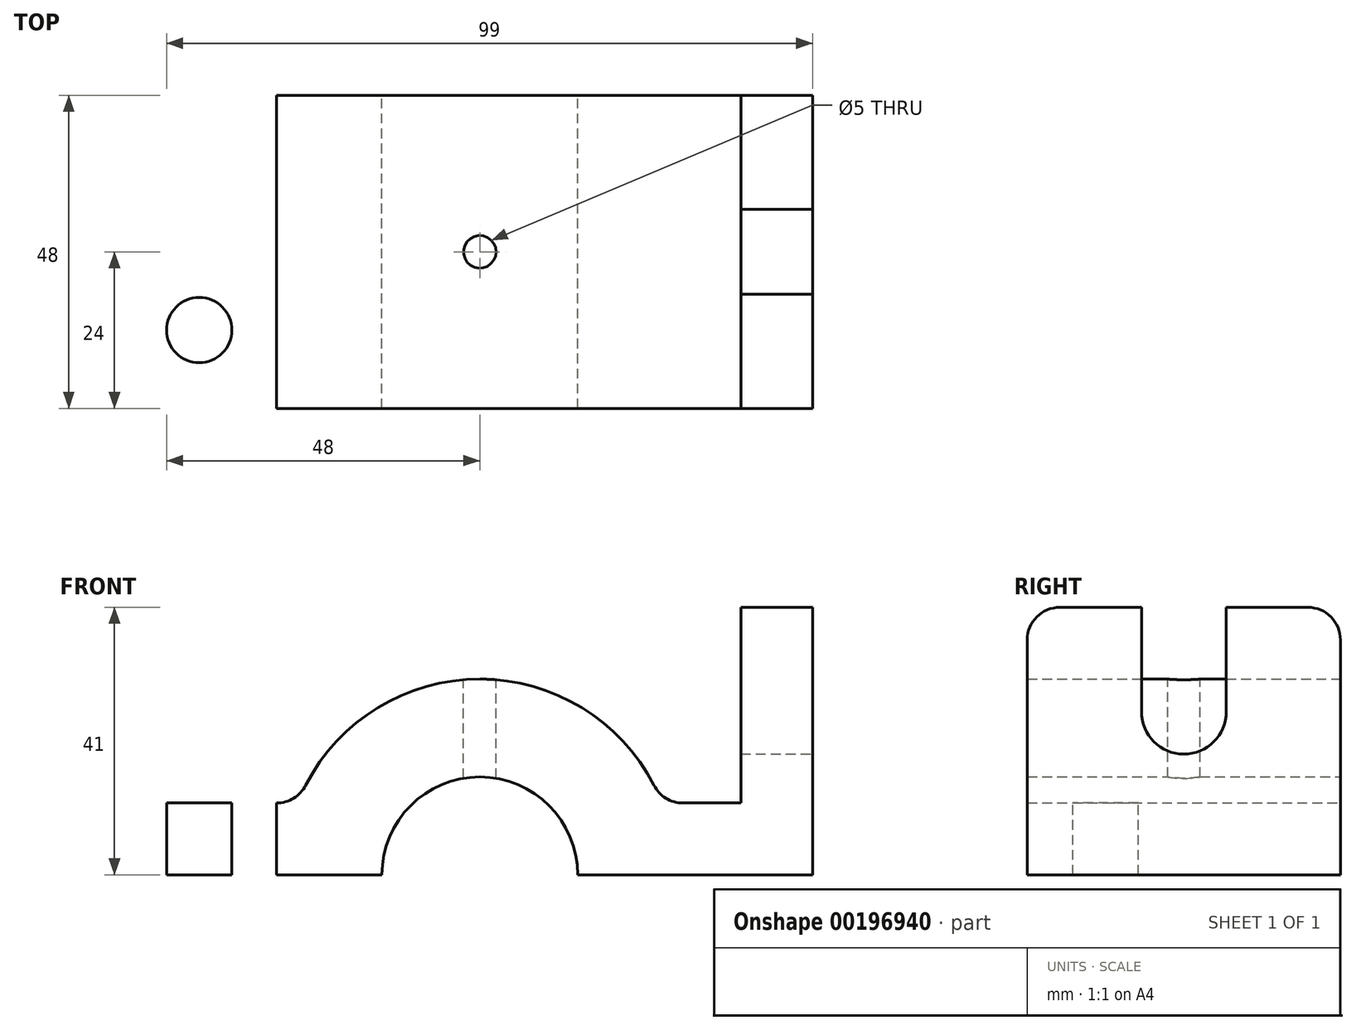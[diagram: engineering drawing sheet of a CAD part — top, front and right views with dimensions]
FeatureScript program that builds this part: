
annotation { "Feature Type Name" : "Feature", "Feature Type Description" : "" }
export const myFeature = defineFeature(function(context is Context, id is Id, definition is map)
    precondition{}
    {
        {
            var Q0;
            Q0=qCreatedBy(makeId("Front.planeOp"),FACE);
            var sketch = newSketch(context, id + "F0", { "sketchPlane" : qUnion([Q0])});
            skArc(sketch, "E0", {"start": v(15, 0) * mm, "mid": v(0, 15) * mm, "end": v(-15, 0) * mm});
            skArc(sketch, "E1", {"start": v(27.91, 11) * mm, "mid": v(0, 30) * mm, "end": v(-27.91, 11) * mm});
            skLineSegment(sketch, "E2", {"start": v(-15, 0) * mm, "end": v(-56, 0) * mm});
            skLineSegment(sketch, "E3", {"start": v(-56, 0) * mm, "end": v(-56, 11) * mm});
            skLineSegment(sketch, "E4", {"start": v(15, 0) * mm, "end": v(51, 0) * mm});
            skLineSegment(sketch, "E5", {"start": v(51, 0) * mm, "end": v(51, 41) * mm});
            skLineSegment(sketch, "E6", {"start": v(51, 41) * mm, "end": v(40, 41) * mm});
            skLineSegment(sketch, "E7", {"start": v(40, 41) * mm, "end": v(40, 11) * mm});
            skLineSegment(sketch, "E8", {"start": v(-56, 11) * mm, "end": v(-27.91, 11) * mm});
            skLineSegment(sketch, "E9.trimOffspring", {"start": v(27.91, 11) * mm, "end": v(40, 11) * mm});
            skSolve(sketch);
        }
        {
            var Q0;
            Q0=makeQuery(id+"F0.imprint","IMPRINT",FACE,{"disambiguationData":[TD([[makeQuery(id+"F0.imprint","IMPRINT",EDGE,{"derivedFrom":sQuery(id+"F0.wireOp",EDGE,"E0")}),-1.0]])]});
            extrude(context, id + "F1", {"entities" : qUnion([Q0]), "depth" : 48 * mm, "symmetric" : true});
        }
        {
            var Q0;
            Q0=makeQuery(id+"F1.opExtrude","CAP_EDGE",EDGE,{"disambiguationData":[OSD([sQuery(id+"F0.wireOp",EDGE,"E3")])],"isStart":false});
            var Q1;
            Q1=makeQuery(id+"F1.opExtrude","CAP_EDGE",EDGE,{"disambiguationData":[OSD([sQuery(id+"F0.wireOp",EDGE,"E3")])],"isStart":true});
            fillet(context, id + "F2", {"entities" : qUnion([Q0, Q1]), "radius" : 13 * mm, "tangentPropagation" : true, "allowEdgeOverflow" : false});
        }
        {
            var Q0;
            Q0=makeQuery(id+"F1.opExtrude","CAP_EDGE",EDGE,{"disambiguationData":[OSD([sQuery(id+"F0.wireOp",EDGE,"E6")])],"isStart":false});
            var Q1;
            Q1=makeQuery(id+"F1.opExtrude","CAP_EDGE",EDGE,{"disambiguationData":[OSD([sQuery(id+"F0.wireOp",EDGE,"E6")])],"isStart":true});
            var Q2;
            Q2=makeQuery(id+"F1.opExtrude","SWEPT_EDGE",EDGE,{"disambiguationData":[OSD([sQuery(id+"F0.wireOp",EDGE,"E1"),sQuery(id+"F0.wireOp",EDGE,"E8")])]});
            var Q3;
            Q3=makeQuery(id+"F1.opExtrude","SWEPT_EDGE",EDGE,{"disambiguationData":[OSD([sQuery(id+"F0.wireOp",EDGE,"E1"),sQuery(id+"F0.wireOp",EDGE,"E9.trimOffspring")])]});
            fillet(context, id + "F3", {"entities" : qUnion([Q0, Q1, Q2, Q3]), "radius" : 5 * mm, "tangentPropagation" : true, "allowEdgeOverflow" : false});
        }
        {
            var Q0;
            Q0=makeQuery(id+"F1.opExtrude","SWEPT_FACE",FACE,{"disambiguationData":[OSD([sQuery(id+"F0.wireOp",EDGE,"E8")])]});
            var sketch = newSketch(context, id + "F4", { "sketchPlane" : qUnion([Q0])});
            skLineSegment(sketch, "E10", {"start": v(-56.94, 0) * mm, "end": v(56.55, 0) * mm, "construction": true});
            skCircle(sketch, "E11", {"center": v(-43, 12) * mm, "radius": 5 * mm});
            skCircle(sketch, "E12.MirrorC", {"center": v(-43, -12) * mm, "radius": 5 * mm});
            skCircle(sketch, "E13", {"center": v(0, 0) * mm, "radius": 2.5 * mm});
            skSolve(sketch);
        }
        {
            var Q0;
            Q0=makeQuery(id+"F4.imprint","IMPRINT",FACE,{"disambiguationData":[TD([[makeQuery(id+"F4.imprint","IMPRINT",EDGE,{"derivedFrom":sQuery(id+"F4.wireOp",EDGE,"E11")}),1.0]])]});
            var Q1;
            Q1=makeQuery(id+"F4.imprint","IMPRINT",FACE,{"disambiguationData":[TD([[makeQuery(id+"F4.imprint","IMPRINT",EDGE,{"derivedFrom":sQuery(id+"F4.wireOp",EDGE,"E12.MirrorC")}),-1.0]])]});
            var Q2;
            Q2=makeQuery(id+"F4.imprint","IMPRINT",FACE,{"disambiguationData":[TD([[makeQuery(id+"F4.imprint","IMPRINT",EDGE,{"derivedFrom":sQuery(id+"F4.wireOp",EDGE,"E13")}),1.0]])]});
            extrude(context, id + "F5", {"entities" : qUnion([Q0, Q1, Q2]), "operationType" : NewBodyOperationType.REMOVE, "oppositeDirection" : true, "depth" : 88.8 * mm, "symmetric" : true});
        }
        {
            var Q0;
            Q0=makeQuery(id+"F1.opExtrude","SWEPT_FACE",FACE,{"disambiguationData":[OSD([sQuery(id+"F0.wireOp",EDGE,"E5")])]});
            var sketch = newSketch(context, id + "F6", { "sketchPlane" : qUnion([Q0])});
            skLineSegment(sketch, "E14.bottom", {"start": v(-6.5, 50.82) * mm, "end": v(6.5, 50.82) * mm});
            skLineSegment(sketch, "E14.top", {"start": v(-6.5, 25) * mm, "end": v(6.5, 25) * mm, "construction": true});
            skLineSegment(sketch, "E14.left", {"start": v(-6.5, 50.82) * mm, "end": v(-6.5, 25) * mm});
            skLineSegment(sketch, "E14.right", {"start": v(6.5, 50.82) * mm, "end": v(6.5, 25) * mm});
            skLineSegment(sketch, "E15", {"start": v(0, 50.82) * mm, "end": v(0, 25) * mm, "construction": true});
            skArc(sketch, "E16", {"start": v(-6.5, 25) * mm, "mid": v(0, 18.5) * mm, "end": v(6.5, 25) * mm});
            skSolve(sketch);
        }
        {
            var Q0;
            {var subQ0=sQuery(id+"F6.wireOp",EDGE,"E16");Q0=makeQuery(id+"F6.imprint","IMPRINT",FACE,{"disambiguationData":[TD([[makeQuery(id+"F6.imprint","IMPRINT",EDGE,{"derivedFrom":subQ0}),1.0]])]});}
            extrude(context, id + "F7", {"entities" : qUnion([Q0]), "operationType" : NewBodyOperationType.REMOVE, "oppositeDirection" : true, "depth" : 15.7 * mm, "hasSecondDirection" : true, "secondDirectionOppositeDirection" : false, "secondDirectionDepth" : 25 * mm});
        }
    });
